# Revit family: QF_ZANUSSI_730294_IGF618M340SNP
name_source: partatom
category: Attrezzature speciali
revit_build: Autodesk Revit 2018 (Build: 20181011_1500(x64)
units: mm (PartAtom-declared; Revit-internal decimal feet)

## family parameters
Basato su piano di lavoro = No
Condiviso = No
Punto di calcolo locali = No
Quota connettore circolare = Usa diametro
Sempre verticale = Sì
Taglio con vuoti quando caricato = No
Tipo di parte = Normale

## types (1)
- Standard
    Accessory = Sì
    Cold Water Size = 19 mm
    Compressed Air Pressure = 0.0 Pa
    Compressed Air Size = 0 mm
    Compressed Air Volume = 0.0 L/s
    Condensate Return Size = 0 mm
    Cycle = 50 Hz
    Depth Actual = 819 mm  [stored 2.68701 ft]
    Descrizione = WATER COOLED GRANULAR ICE 618KG/24H-BIN 340KG MODULAR
    Gas Input Pressure = 0
    Gas KW = 0
    Gas Size = 0 mm
    HP = 2.3 HP
    Height Actual = 1972 mm  [stored 6.46982 ft]
    Hot Water Size = 0 mm
    Item Number = 730294
    Length Actual = 762 mm  [stored 2.5 ft]
    Modello = IGF618M340SNP
    Phase = 1
    Produttore = Zanussi
    Refrigerant Compressor Remote = Sì
    Refrigeration Liquid Line Size = 0 mm  [stored 0 ft]
    Refrigeration Suction Line Size = 0 mm  [stored 0 ft]
    Steam Pounds per Hour = 0
    Steam Supply Maximum Pressure = 0.0 Pa
    Steam Supply Minimum Pressure = 0.0 Pa
    Steam Supply Size = 0 mm
    URL = http://www.zanussiprofessional.com
    URL Manufacturer = http://www.zanussiprofessional.com
    Volts = 200 V
    Watts = 1700 W
    Weight = 52.00 kg

note: source unit labels omitted for Gas Input Pressure — the stored unit's dimension contradicts the parameter name (converter mislabeling)

note: [stored X ft] marks values corroborated as IEEE doubles in the binary element streams (Revit-internal decimal feet)
